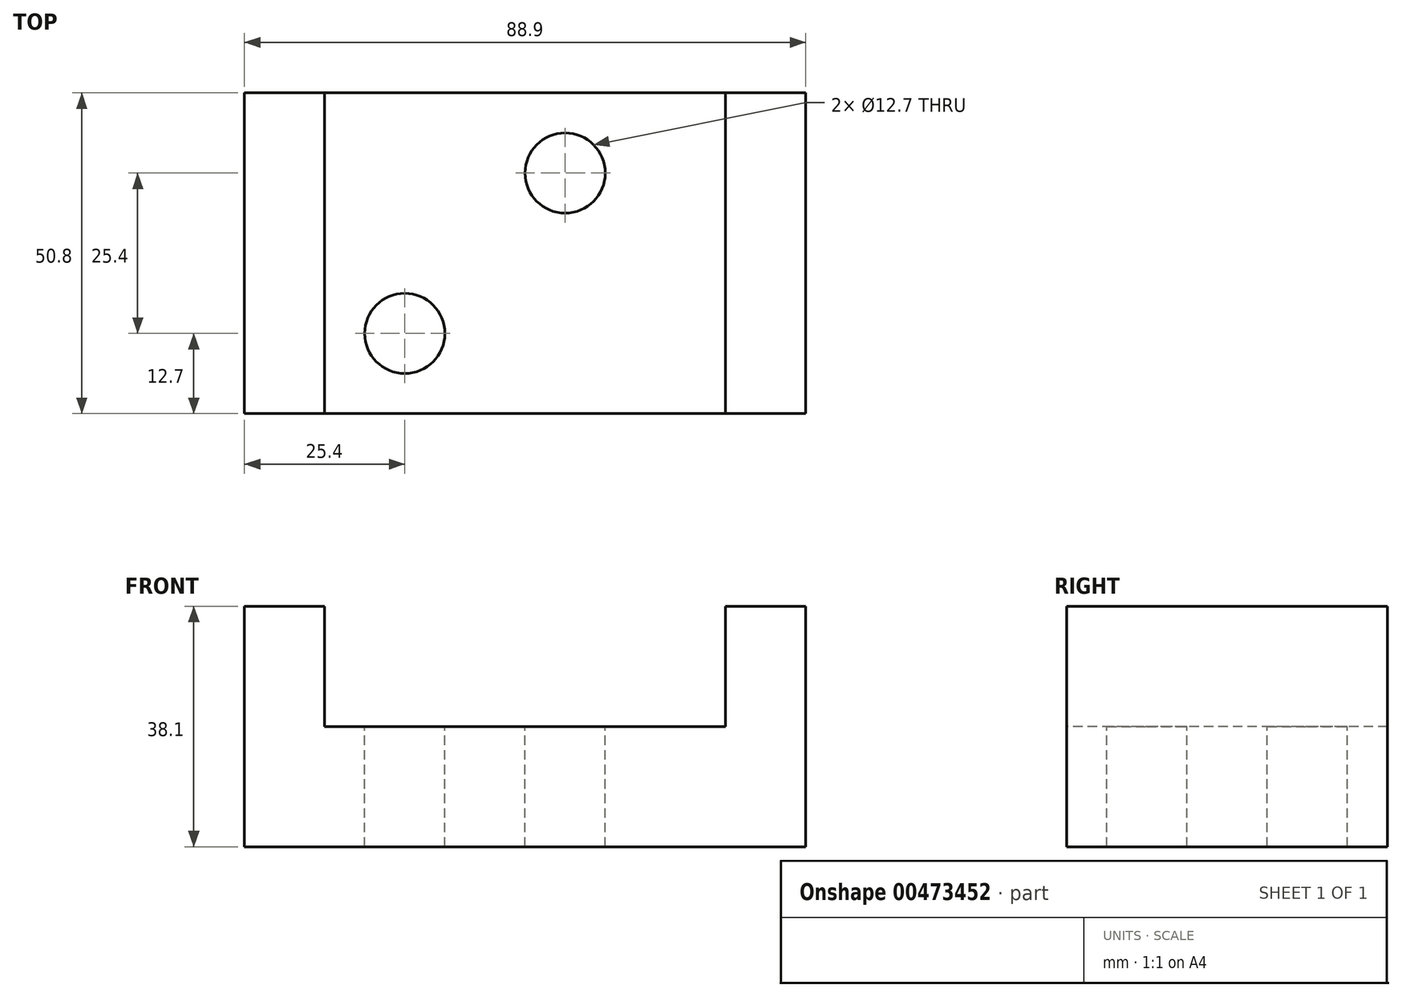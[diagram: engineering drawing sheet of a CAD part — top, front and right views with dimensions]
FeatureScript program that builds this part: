
annotation { "Feature Type Name" : "Feature", "Feature Type Description" : "" }
export const myFeature = defineFeature(function(context is Context, id is Id, definition is map)
    precondition{}
    {
        {
            var Q0;
            Q0=qCreatedBy(makeId("Front.planeOp"),FACE);
            var sketch = newSketch(context, id + "F0", { "sketchPlane" : qUnion([Q0])});
            skLineSegment(sketch, "E0.bottom", {"start": v(-44.45, -19.05) * mm, "end": v(44.45, -19.05) * mm});
            skLineSegment(sketch, "E0.top", {"start": v(-44.45, 19.05) * mm, "end": v(44.45, 19.05) * mm});
            skLineSegment(sketch, "E0.left", {"start": v(-44.45, -19.05) * mm, "end": v(-44.45, 19.05) * mm});
            skLineSegment(sketch, "E0.right", {"start": v(44.45, -19.05) * mm, "end": v(44.45, 19.05) * mm});
            skPoint(sketch, "E0.middle", {"position": v(0, 0) * mm});
            skSolve(sketch);
        }
        {
            var Q0;
            Q0 = qSketchRegion(id + "F0", true);
            extrude(context, id + "F1", {"entities" : qUnion([Q0]), "depth" : 50.8 * mm});
        }
        {
            var Q0;
            Q0=makeQuery(id+"F1.opExtrude","CAP_FACE",FACE,{"disambiguationData":[OSD([sQuery(id+"F0.wireOp",EDGE,"E0.bottom"),sQuery(id+"F0.wireOp",EDGE,"E0.top"),sQuery(id+"F0.wireOp",EDGE,"E0.left"),sQuery(id+"F0.wireOp",EDGE,"E0.right")])],"isStart":false});
            var sketch = newSketch(context, id + "F2", { "sketchPlane" : qUnion([Q0])});
            skLineSegment(sketch, "E1.bottom", {"start": v(-31.75, 19.05) * mm, "end": v(31.75, 19.05) * mm});
            skLineSegment(sketch, "E1.top", {"start": v(-31.75, 0) * mm, "end": v(31.75, 0) * mm});
            skLineSegment(sketch, "E1.left", {"start": v(-31.75, 19.05) * mm, "end": v(-31.75, 0) * mm});
            skLineSegment(sketch, "E1.right", {"start": v(31.75, 19.05) * mm, "end": v(31.75, 0) * mm});
            skSolve(sketch);
        }
        {
            var Q0;
            Q0 = qSketchRegion(id + "F2", true);
            extrude(context, id + "F3", {"entities" : qUnion([Q0]), "operationType" : NewBodyOperationType.REMOVE, "endBound" : BoundingType.THROUGH_ALL, "oppositeDirection" : true, "depth" : 25.4 * mm});
        }
        {
            var Q0;
            Q0=makeQuery(id+"F3.boolean.opBoolean","COPY",FACE,{"derivedFrom":makeQuery(id+"F3.opExtrude","SWEPT_FACE",FACE,{"disambiguationData":[OSD([sQuery(id+"F2.wireOp",EDGE,"E1.top")])]})});
            var sketch = newSketch(context, id + "F4", { "sketchPlane" : qUnion([Q0])});
            skCircle(sketch, "E2", {"center": v(-19.05, -38.1) * mm, "radius": 6.35 * mm});
            skSolve(sketch);
        }
        {
            var Q0;
            Q0 = qSketchRegion(id + "F4", true);
            extrude(context, id + "F5", {"entities" : qUnion([Q0]), "operationType" : NewBodyOperationType.REMOVE, "endBound" : BoundingType.THROUGH_ALL, "oppositeDirection" : true, "depth" : 25.4 * mm});
        }
        {
            var Q0;
            Q0=makeQuery(id+"F3.boolean.opBoolean","COPY",FACE,{"derivedFrom":makeQuery(id+"F3.opExtrude","SWEPT_FACE",FACE,{"disambiguationData":[OSD([sQuery(id+"F2.wireOp",EDGE,"E1.top")])]})});
            var sketch = newSketch(context, id + "F6", { "sketchPlane" : qUnion([Q0])});
            skCircle(sketch, "E3", {"center": v(6.35, -12.7) * mm, "radius": 6.35 * mm});
            skSolve(sketch);
        }
        {
            var Q0;
            Q0 = qSketchRegion(id + "F6", true);
            extrude(context, id + "F7", {"entities" : qUnion([Q0]), "operationType" : NewBodyOperationType.REMOVE, "endBound" : BoundingType.THROUGH_ALL, "oppositeDirection" : true, "depth" : 25.4 * mm});
        }
    });
